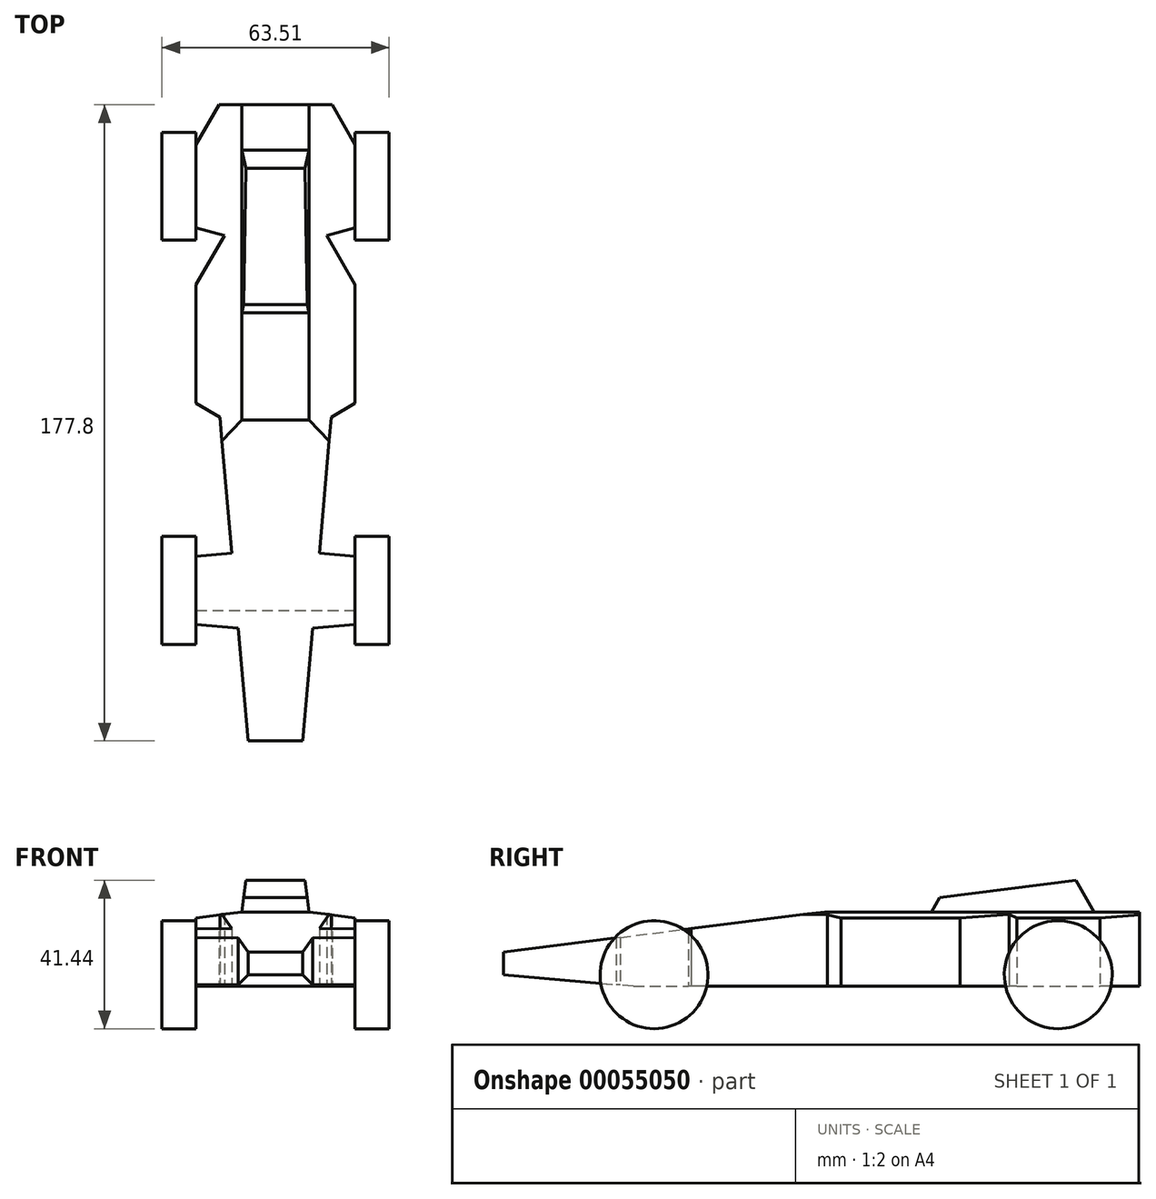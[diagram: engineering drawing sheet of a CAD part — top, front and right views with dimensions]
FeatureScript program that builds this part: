
annotation { "Feature Type Name" : "Feature", "Feature Type Description" : "" }
export const myFeature = defineFeature(function(context is Context, id is Id, definition is map)
    precondition{}
    {
        {
            var Q0;
            Q0=qCreatedBy(makeId("Top.planeOp"),FACE);
            var sketch = newSketch(context, id + "F0", { "sketchPlane" : qUnion([Q0])});
            skLineSegment(sketch, "E0.bottom", {"start": v(0, 0) * mm, "end": v(44.45, 0) * mm});
            skLineSegment(sketch, "E0.top", {"start": v(0, 177.8) * mm, "end": v(44.45, 177.8) * mm});
            skLineSegment(sketch, "E0.left", {"start": v(0, 0) * mm, "end": v(0, 177.8) * mm});
            skLineSegment(sketch, "E0.right", {"start": v(44.45, 0) * mm, "end": v(44.45, 177.8) * mm});
            skPoint(sketch, "E1", {"position": v(22.22, 177.8) * mm});
            skPoint(sketch, "E2", {"position": v(22.22, 34.92) * mm});
            skLineSegment(sketch, "E3", {"start": v(22.22, 34.92) * mm, "end": v(22.22, 34.92) * mm});
            skLineSegment(sketch, "E4", {"start": v(22.22, 177.8) * mm, "end": v(22.22, 34.92) * mm, "construction": true});
            skPoint(sketch, "E5.orphan", {"position": v(23.02, 34.92) * mm});
            skPoint(sketch, "E6.start.orphan", {"position": v(21.43, 34.92) * mm});
            skSolve(sketch);
        }
        {
            var Q0;
            Q0=makeQuery(id+"F0.imprint","IMPRINT",FACE,{"disambiguationData":[TD([[makeQuery(id+"F0.imprint","IMPRINT",EDGE,{"derivedFrom":sQuery(id+"F0.wireOp",EDGE,"E0.bottom")}),1.0]])]});
            extrude(context, id + "F16", {"entities" : qUnion([Q0]), "depth" : 31.75 * mm});
        }
        {
            var Q0;
            Q0=makeQuery(id+"F16.opExtrude","SWEPT_FACE",FACE,{"disambiguationData":[OSD([sQuery(id+"F0.wireOp",EDGE,"E0.right")])]});
            var sketch = newSketch(context, id + "F1", { "sketchPlane" : qUnion([Q0])});
            skLineSegment(sketch, "E7.bottom", {"start": v(41.28, 0) * mm, "end": v(42.86, 0) * mm});
            skLineSegment(sketch, "E7.top", {"start": v(41.28, 3.18) * mm, "end": v(42.86, 3.18) * mm});
            skLineSegment(sketch, "E7.left", {"start": v(41.28, 0) * mm, "end": v(41.28, 3.18) * mm});
            skLineSegment(sketch, "E7.right", {"start": v(42.86, 0) * mm, "end": v(42.86, 3.18) * mm});
            skLineSegment(sketch, "E8.bottom", {"start": v(152.4, 0) * mm, "end": v(153.99, 0) * mm});
            skLineSegment(sketch, "E8.top", {"start": v(152.4, 3.18) * mm, "end": v(153.99, 3.18) * mm});
            skLineSegment(sketch, "E8.left", {"start": v(152.4, 0) * mm, "end": v(152.4, 3.18) * mm});
            skLineSegment(sketch, "E8.right", {"start": v(153.99, 0) * mm, "end": v(153.99, 3.18) * mm});
            skSolve(sketch);
        }
        {
            var Q0;
            Q0=makeQuery(id+"F16.opExtrude","SWEPT_FACE",FACE,{"disambiguationData":[OSD([sQuery(id+"F0.wireOp",EDGE,"E0.right")])]});
            var sketch = newSketch(context, id + "F2", { "sketchPlane" : qUnion([Q0])});
            skLineSegment(sketch, "E9", {"start": v(0, 31.75) * mm, "end": v(0, 9.52) * mm});
            skLineSegment(sketch, "E10", {"start": v(0, 9.52) * mm, "end": v(177.8, 31.75) * mm});
            skLineSegment(sketch, "E11", {"start": v(0, 31.75) * mm, "end": v(177.8, 31.75) * mm});
            skSolve(sketch);
        }
        {
            var Q0;
            Q0 = qSketchRegion(id + "F2", true);
            extrude(context, id + "F3", {"entities" : qUnion([Q0]), "operationType" : NewBodyOperationType.REMOVE, "endBound" : BoundingType.UP_TO_NEXT, "oppositeDirection" : true, "depth" : 25.4 * mm});
        }
        {
            var Q0;
            {var subQ0=sQuery(id+"F0.wireOp",EDGE,"E0.left");var subQ1=sQuery(id+"F0.wireOp",EDGE,"E0.right");Q0=makeQuery(id+"FpUXt2tdTj9OgTn2d_1.boolean.opBoolean","SPLIT",FACE,{"disambiguationData":[TD([makeQuery(id+"FpUXt2tdTj9OgTn2d_1.opExtrude","SWEPT_FACE",FACE,{"disambiguationData":[OSD([sQuery(id+"F1.wireOp",EDGE,"E7.right")])]})])],"derivedFrom":makeQuery(id+"F16.opExtrude","CAP_FACE",FACE,{"disambiguationData":[OSD([sQuery(id+"F0.wireOp",EDGE,"E0.bottom"),sQuery(id+"F0.wireOp",EDGE,"E0.top"),subQ0,subQ1])],"isStart":true})});}
            var Q1;
            Q1=makeQuery(id+"F16.opExtrude","SWEPT_FACE",FACE,{"disambiguationData":[OSD([sQuery(id+"F0.wireOp",EDGE,"E0.left")])]});
            var sketch = newSketch(context, id + "F4", { "sketchPlane" : qUnion([Q0, Q1])});
            skLineSegment(sketch, "E12", {"start": v(14.58, 0) * mm, "end": v(14.58, 0) * mm});
            skLineSegment(sketch, "E13", {"start": v(14.58, 0) * mm, "end": v(0, 0) * mm});
            skLineSegment(sketch, "E14", {"start": v(0, -32.54) * mm, "end": v(0, 0) * mm});
            skLineSegment(sketch, "E15", {"start": v(10, -52.47) * mm, "end": v(0, -51.6) * mm});
            skLineSegment(sketch, "E16", {"start": v(0, -143.41) * mm, "end": v(0, -51.6) * mm});
            skLineSegment(sketch, "E17", {"start": v(11.83, -31.5) * mm, "end": v(0, -32.54) * mm});
            skLineSegment(sketch, "E18", {"start": v(0, -32.54) * mm, "end": v(0, -51.6) * mm, "construction": true});
            skPoint(sketch, "E19", {"position": v(0, -42.07) * mm});
            skLineSegment(sketch, "E20", {"start": v(0, -42.86) * mm, "end": v(0, -41.27) * mm, "construction": true});
            skLineSegment(sketch, "E21", {"start": v(0, -143.41) * mm, "end": v(7.94, -141.29) * mm});
            skLineSegment(sketch, "E22", {"start": v(6.67, -90.49) * mm, "end": v(10, -52.47) * mm});
            skLineSegment(sketch, "E23", {"start": v(11.83, -31.5) * mm, "end": v(14.58, 0) * mm});
            skPoint(sketch, "E24", {"position": v(0, -166.69) * mm});
            skLineSegment(sketch, "E25", {"start": v(22.22, 0) * mm, "end": v(22.22, -177.8) * mm, "construction": true});
            skLineSegment(sketch, "E26.MirrorCS", {"start": v(29.87, 0) * mm, "end": v(44.45, 0) * mm});
            skLineSegment(sketch, "E27.MirrorCS", {"start": v(44.45, -32.54) * mm, "end": v(44.45, 0) * mm});
            skLineSegment(sketch, "E28.MirrorCS", {"start": v(32.62, -31.5) * mm, "end": v(44.45, -32.54) * mm});
            skLineSegment(sketch, "E29.MirrorCS", {"start": v(44.45, -143.41) * mm, "end": v(44.45, -51.6) * mm});
            skLineSegment(sketch, "E30.MirrorCS", {"start": v(34.46, -52.47) * mm, "end": v(44.45, -51.6) * mm});
            skLineSegment(sketch, "E31.MirrorCS", {"start": v(44.45, -143.41) * mm, "end": v(36.51, -141.29) * mm});
            skLineSegment(sketch, "E32.MirrorCS", {"start": v(32.62, -31.5) * mm, "end": v(29.87, 0) * mm});
            skLineSegment(sketch, "E33", {"start": v(0, -127.54) * mm, "end": v(7.94, -141.29) * mm});
            skLineSegment(sketch, "E34", {"start": v(0, -127.54) * mm, "end": v(0, -94.34) * mm, "construction": true});
            skLineSegment(sketch, "E35", {"start": v(0, -94.34) * mm, "end": v(6.67, -90.49) * mm});
            skPoint(sketch, "E36.MirrorCS.end.orphan", {"position": v(34.46, -52.47) * mm});
            skPoint(sketch, "E36.MirrorCS.start.orphan", {"position": v(36.51, -141.29) * mm});
            skLineSegment(sketch, "E37.MirrorCS", {"start": v(37.78, -90.49) * mm, "end": v(34.46, -52.47) * mm});
            skLineSegment(sketch, "E38.MirrorCS", {"start": v(44.45, -94.34) * mm, "end": v(37.78, -90.49) * mm});
            skLineSegment(sketch, "E39.MirrorCS", {"start": v(44.45, -127.54) * mm, "end": v(44.45, -94.34) * mm, "construction": true});
            skLineSegment(sketch, "E40.MirrorCS", {"start": v(44.45, -127.54) * mm, "end": v(36.51, -141.29) * mm});
            skLineSegment(sketch, "E41", {"start": v(0, -166.69) * mm, "end": v(0, -166.69) * mm});
            skLineSegment(sketch, "E42", {"start": v(0, -166.69) * mm, "end": v(0, -177.8) * mm});
            skLineSegment(sketch, "E43", {"start": v(0, -177.8) * mm, "end": v(6.42, -177.8) * mm});
            skLineSegment(sketch, "E44", {"start": v(6.42, -177.8) * mm, "end": v(0, -166.69) * mm});
            skLineSegment(sketch, "E45.MirrorCS", {"start": v(44.45, -166.69) * mm, "end": v(44.45, -177.8) * mm});
            skLineSegment(sketch, "E46.MirrorCS", {"start": v(38.03, -177.8) * mm, "end": v(44.45, -166.69) * mm});
            skLineSegment(sketch, "E47.MirrorCS", {"start": v(44.45, -166.69) * mm, "end": v(44.45, -166.69) * mm});
            skLineSegment(sketch, "E48.MirrorCS", {"start": v(44.45, -177.8) * mm, "end": v(38.03, -177.8) * mm});
            skSolve(sketch);
        }
        {
            var Q0;
            Q0 = qSketchRegion(id + "F4", true);
            extrude(context, id + "F5", {"entities" : qUnion([Q0]), "operationType" : NewBodyOperationType.REMOVE, "endBound" : BoundingType.UP_TO_NEXT, "oppositeDirection" : true, "depth" : 25.4 * mm});
        }
        {
            var Q0;
            Q0=makeQuery(id+"F16.opExtrude","SWEPT_FACE",FACE,{"disambiguationData":[OSD([sQuery(id+"F0.wireOp",EDGE,"E0.top")])]});
            var sketch = newSketch(context, id + "F6", { "sketchPlane" : qUnion([Q0])});
            skLineSegment(sketch, "E49", {"start": v(-30.16, 31.75) * mm, "end": v(-31.61, 20.74) * mm});
            skLineSegment(sketch, "E50", {"start": v(-31.61, 20.74) * mm, "end": v(-44.45, 19.05) * mm});
            skLineSegment(sketch, "E51", {"start": v(-44.45, 19.05) * mm, "end": v(-44.45, 31.75) * mm});
            skLineSegment(sketch, "E52", {"start": v(-44.45, 31.75) * mm, "end": v(-30.16, 31.75) * mm});
            skLineSegment(sketch, "E53", {"start": v(-22.22, 31.75) * mm, "end": v(-22.22, 0) * mm, "construction": true});
            skLineSegment(sketch, "E54.MirrorCS", {"start": v(-14.29, 31.75) * mm, "end": v(-12.84, 20.74) * mm});
            skLineSegment(sketch, "E55.MirrorCS", {"start": v(-12.84, 20.74) * mm, "end": v(0, 19.05) * mm});
            skLineSegment(sketch, "E56.MirrorCS", {"start": v(0, 19.05) * mm, "end": v(0, 31.75) * mm});
            skLineSegment(sketch, "E57.MirrorCS", {"start": v(0, 31.75) * mm, "end": v(-14.29, 31.75) * mm});
            skSolve(sketch);
        }
        {
            var Q0;
            Q0 = qSketchRegion(id + "F6", true);
            extrude(context, id + "F7", {"entities" : qUnion([Q0]), "operationType" : NewBodyOperationType.REMOVE, "endBound" : BoundingType.UP_TO_NEXT, "oppositeDirection" : true, "depth" : 25.4 * mm});
        }
        {
            var Q0;
            Q0=qCreatedBy(makeId("Right.planeOp"),FACE);
            var sketch = newSketch(context, id + "F17", { "sketchPlane" : qUnion([Q0])});
            skLineSegment(sketch, "E58", {"start": v(165.1, 20.74) * mm, "end": v(160.03, 29.53) * mm});
            skLineSegment(sketch, "E59", {"start": v(160.03, 29.53) * mm, "end": v(177.8, 31.75) * mm});
            skLineSegment(sketch, "E60", {"start": v(177.8, 20.74) * mm, "end": v(177.8, 31.75) * mm});
            skLineSegment(sketch, "E61", {"start": v(119.6, 20.74) * mm, "end": v(121.93, 24.77) * mm});
            skLineSegment(sketch, "E62", {"start": v(121.93, 24.77) * mm, "end": v(89.72, 20.74) * mm});
            skLineSegment(sketch, "E63", {"start": v(89.72, 20.74) * mm, "end": v(119.6, 20.74) * mm});
            skLineSegment(sketch, "E64", {"start": v(165.1, 20.74) * mm, "end": v(177.8, 20.74) * mm});
            skSolve(sketch);
        }
        {
            var Q0;
            Q0 = qSketchRegion(id + "F17", true);
            extrude(context, id + "F18", {"entities" : qUnion([Q0]), "operationType" : NewBodyOperationType.REMOVE, "endBound" : BoundingType.THROUGH_ALL, "depth" : 25.4 * mm});
        }
        {
            var Q0;
            Q0=qCreatedBy(makeId("Right.planeOp"),FACE);
            var sketch = newSketch(context, id + "F8", { "sketchPlane" : qUnion([Q0])});
            skLineSegment(sketch, "E65", {"start": v(0, 0) * mm, "end": v(36.3, 0) * mm});
            skLineSegment(sketch, "E66", {"start": v(36.3, 0) * mm, "end": v(0, 3.17) * mm});
            skLineSegment(sketch, "E67", {"start": v(0, 3.18) * mm, "end": v(0, 0) * mm});
            skSolve(sketch);
        }
        {
            var Q0;
            Q0 = qSketchRegion(id + "F8", true);
            extrude(context, id + "F9", {"entities" : qUnion([Q0]), "operationType" : NewBodyOperationType.REMOVE, "endBound" : BoundingType.THROUGH_ALL, "depth" : 25.4 * mm});
        }
        {
            var Q0;
            {var subQ0=sQuery(id+"F0.wireOp",EDGE,"E0.left");Q0=makeQuery(id+"F5.boolean.opBoolean","SPLIT",FACE,{"disambiguationData":[TD([makeQuery(id+"F5.opExtrude","SWEPT_FACE",FACE,{"disambiguationData":[OSD([sQuery(id+"F4.wireOp",EDGE,"E21")])]})])],"derivedFrom":makeQuery(id+"F16.opExtrude","SWEPT_FACE",FACE,{"disambiguationData":[OSD([subQ0])]})});}
            var sketch = newSketch(context, id + "F10", { "sketchPlane" : qUnion([Q0])});
            skCircle(sketch, "E68", {"center": v(-155.05, 3.18) * mm, "radius": 15.08 * mm});
            skPoint(sketch, "E69", {"position": v(-155.05, 0) * mm});
            skLineSegment(sketch, "E70", {"start": v(-51.6, 3.18) * mm, "end": v(-32.54, 3.18) * mm, "construction": true});
            skPoint(sketch, "E71", {"position": v(-42.07, 3.18) * mm});
            skCircle(sketch, "E72", {"center": v(-42.07, 3.18) * mm, "radius": 15.08 * mm});
            skSolve(sketch);
        }
        {
            var Q0;
            Q0 = qSketchRegion(id + "F10", true);
            extrude(context, id + "F11", {"entities" : qUnion([Q0]), "operationType" : NewBodyOperationType.ADD, "depth" : 9.52 * mm});
        }
        {
            var Q0;
            {var subQ0=sQuery(id+"F0.wireOp",EDGE,"E0.right");Q0=makeQuery(id+"F5.boolean.opBoolean","SPLIT",FACE,{"disambiguationData":[TD([makeQuery(id+"F5.opExtrude","SWEPT_FACE",FACE,{"disambiguationData":[OSD([sQuery(id+"F4.wireOp",EDGE,"E31.MirrorCS")])]})])],"derivedFrom":makeQuery(id+"F16.opExtrude","SWEPT_FACE",FACE,{"disambiguationData":[OSD([subQ0])]})});}
            var sketch = newSketch(context, id + "F12", { "sketchPlane" : qUnion([Q0])});
            skCircle(sketch, "E73", {"center": v(42.07, 3.18) * mm, "radius": 15.08 * mm});
            skCircle(sketch, "E74", {"center": v(155.05, 3.18) * mm, "radius": 15.08 * mm});
            skSolve(sketch);
        }
        {
            var Q0;
            Q0 = qSketchRegion(id + "F12", true);
            extrude(context, id + "F13", {"entities" : qUnion([Q0]), "operationType" : NewBodyOperationType.ADD, "depth" : 9.52 * mm});
        }
        {
            var Q0;
            Q0=sQuery(id+"F0.wireOp",EDGE,"E4");
            cPlane(context, id + "F14", {"entities" : qUnion([Q0]), "cplaneType" : CPlaneType.LINE_ANGLE, "offset" : 25.4 * mm, "angle" : 90 * degree, "flipAlignment" : true, "width" : 152.4 * mm, "height" : 152.4 * mm});
        }
    });
